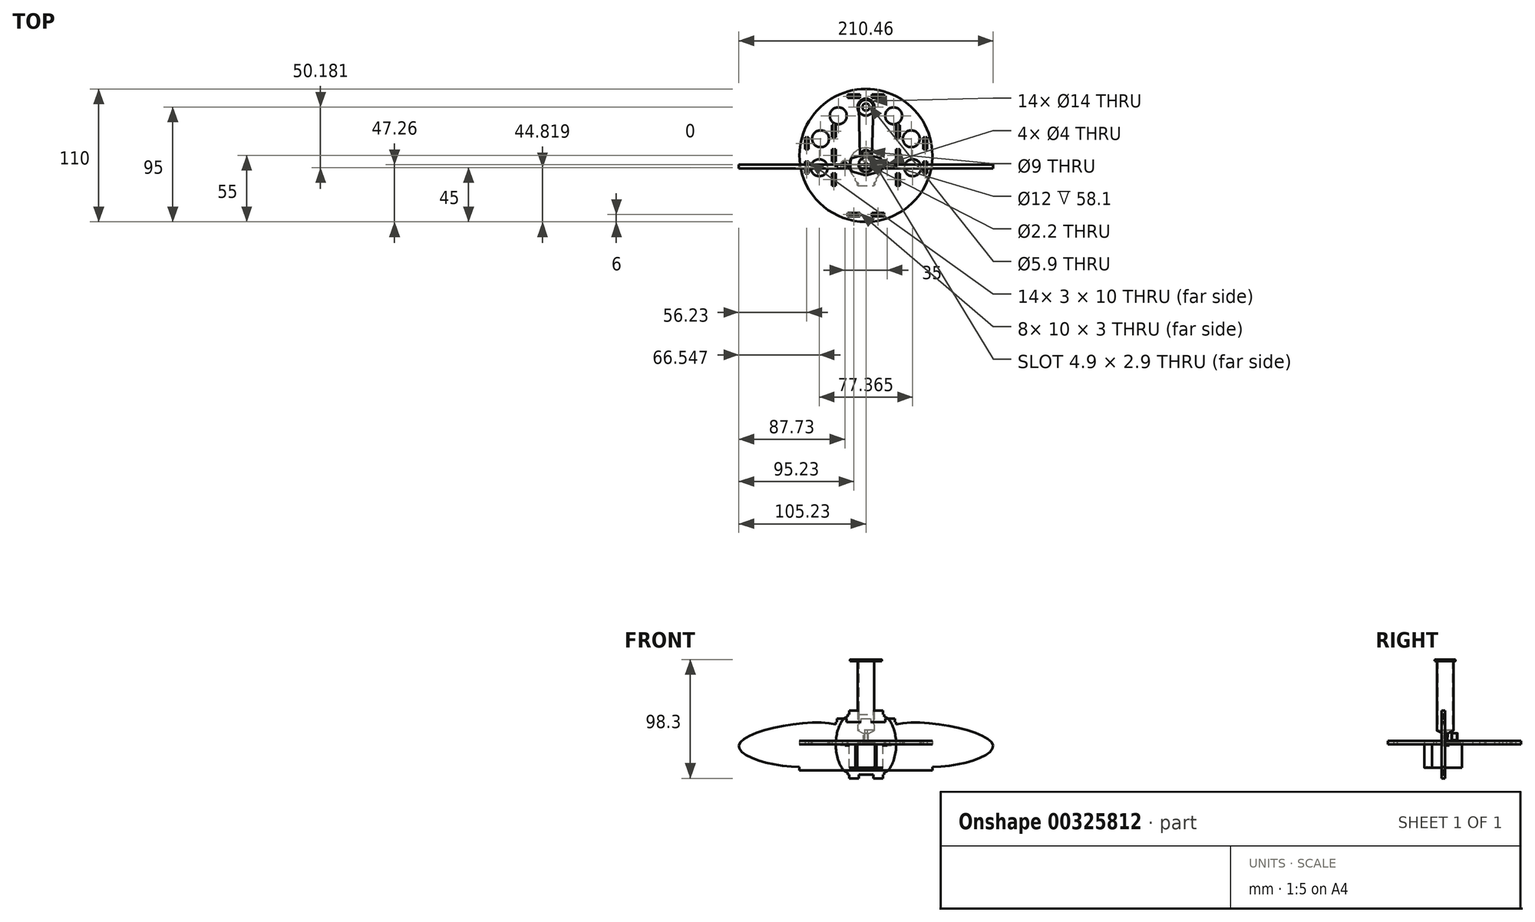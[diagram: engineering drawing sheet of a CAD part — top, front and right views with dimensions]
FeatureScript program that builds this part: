
annotation { "Feature Type Name" : "Feature", "Feature Type Description" : "" }
export const myFeature = defineFeature(function(context is Context, id is Id, definition is map)
    precondition{}
    {
        {
            var Q0;
            Q0=qCreatedBy(makeId("Top.planeOp"),FACE);
            var sketch = newSketch(context, id + "F0", { "sketchPlane" : qUnion([Q0])});
            skCircle(sketch, "E0", {"center": v(0, 0) * mm, "radius": 6.85 * mm});
            skCircle(sketch, "E1", {"center": v(0, 0) * mm, "radius": 1.1 * mm});
            skCircle(sketch, "E2", {"center": v(0, 0) * mm, "radius": 8.5 * mm});
            skLineSegment(sketch, "E3", {"start": v(-1.1, 0) * mm, "end": v(1.1, 0) * mm});
            skLineSegment(sketch, "E4", {"start": v(-11.5, 5.5) * mm, "end": v(-11.4, 5.5) * mm});
            skLineSegment(sketch, "E5", {"start": v(11.5, -5.5) * mm, "end": v(11.4, -5.5) * mm});
            skLineSegment(sketch, "E6", {"start": v(-11.5, 5.5) * mm, "end": v(-2.38, 8.16) * mm});
            skLineSegment(sketch, "E7", {"start": v(-11.5, -5.5) * mm, "end": v(-2.38, -8.16) * mm});
            skLineSegment(sketch, "E8", {"start": v(11.5, -5.5) * mm, "end": v(2.38, -8.16) * mm});
            skLineSegment(sketch, "E9", {"start": v(11.5, 5.5) * mm, "end": v(2.38, 8.16) * mm});
            skFitSpline(sketch, "E10", {"points": [v(-11.5, 5.5) * mm, v(-13.25, 0) * mm, v(-11.5, -5.5) * mm, v(-8.5, 0) * mm, v(-11.5, 5.5) * mm]});
            skFitSpline(sketch, "E11", {"points": [v(11.5, 5.5) * mm, v(13.25, 0) * mm, v(11.5, -5.5) * mm, v(8.5, 0) * mm, v(11.5, 5.5) * mm]});
            skLineSegment(sketch, "E12.trimOffspring", {"start": v(-11.4, -5.5) * mm, "end": v(-11.5, -5.5) * mm});
            skLineSegment(sketch, "E13.trimOffspring", {"start": v(11.4, 5.5) * mm, "end": v(11.5, 5.5) * mm});
            skCircle(sketch, "E14", {"center": v(0, 0) * mm, "radius": 6 * mm});
            skCircle(sketch, "E15", {"center": v(0, 0) * mm, "radius": 2 * mm});
            skSolve(sketch);
        }
        {
            var Q0;
            Q0 = qSketchRegion(id + "F0", true);
            extrude(context, id + "F1", {"entities" : qUnion([Q0]), "depth" : 70.3 * mm});
        }
        {
            var Q0;
            Q0 = qSketchRegion(id + "F0", true);
            extrude(context, id + "F2", {"entities" : qUnion([Q0]), "operationType" : NewBodyOperationType.REMOVE, "depth" : (70.3 - 1.4) * mm});
        }
        {
            var Q0;
            Q0=makeQuery(id+"F0.imprint","IMPRINT",FACE,{"disambiguationData":[TD([[makeQuery(id+"F0.imprint","IMPRINT",EDGE,{"derivedFrom":sQuery(id+"F0.wireOp",EDGE,"E0")}),1.0]])]});
            extrude(context, id + "F3", {"entities" : qUnion([Q0]), "operationType" : NewBodyOperationType.ADD, "depth" : 70.3 * mm, "hasSecondDirection" : true, "secondDirectionOppositeDirection" : true, "secondDirectionDepth" : -9 * mm});
        }
        {
            var Q0;
            Q0=makeQuery(id+"F0.imprint","IMPRINT",FACE,{"disambiguationData":[TD([[makeQuery(id+"F0.imprint","IMPRINT",EDGE,{"derivedFrom":sQuery(id+"F0.wireOp",EDGE,"E14")}),1.0]])]});
            extrude(context, id + "F4", {"entities" : qUnion([Q0]), "operationType" : NewBodyOperationType.ADD, "depth" : 12 * mm, "hasSecondDirection" : true, "secondDirectionOppositeDirection" : true, "secondDirectionDepth" : -9 * mm});
        }
        {
            var Q0;
            Q0=makeQuery(id+"F0.imprint","IMPRINT",FACE,{"disambiguationData":[TD([[makeQuery(id+"F0.imprint","IMPRINT",EDGE,{"derivedFrom":sQuery(id+"F0.wireOp",EDGE,"E15")}),1.0]])]});
            extrude(context, id + "F5", {"entities" : qUnion([Q0]), "operationType" : NewBodyOperationType.ADD, "depth" : 12 * mm});
        }
        {
            var Q0;
            Q0=makeQuery(id+"F3.opExtrude","CAP_EDGE",EDGE,{"disambiguationData":[OSD([sQuery(id+"F0.wireOp",EDGE,"E0")])],"isStart":true});
            chamfer(context, id + "F6", {"entities" : qUnion([Q0]), "chamferType" : ChamferType.TWO_OFFSETS, "width1" : 2.5 * mm, "oppositeDirection" : false, "width2" : 4.9 * mm, "tangentPropagation" : true});
        }
        {
            var Q0;
            Q0=makeQuery(id+"F5.opExtrude","CAP_EDGE",EDGE,{"disambiguationData":[OSD([sQuery(id+"F0.wireOp",EDGE,"E15")])],"isStart":true});
            chamfer(context, id + "F7", {"entities" : qUnion([Q0]), "chamferType" : ChamferType.TWO_OFFSETS, "width1" : 9 * mm, "oppositeDirection" : false, "width2" : 0.1 * mm, "tangentPropagation" : true});
        }
        {
            var Q0;
            Q0=makeQuery(id+"F5.opExtrude","CAP_EDGE",EDGE,{"disambiguationData":[OSD([sQuery(id+"F0.wireOp",EDGE,"E1")])],"isStart":true});
            var Q1;
            {var subQ0=sQuery(id+"F0.wireOp",EDGE,"E15");Q1=makeQuery(id+"F7.opChamfer","BLEND_EDGE",EDGE,{"blendedFrom":[makeQuery(id+"F5.opExtrude","CAP_EDGE",EDGE,{"disambiguationData":[OSD([subQ0])],"isStart":true}),makeQuery(id+"F5.opExtrude","CAP_FACE",FACE,{"disambiguationData":[OSD([sQuery(id+"F0.wireOp",EDGE,"E1"),subQ0])],"isStart":true})],"blendedInto":[makeQuery(id+"F5.opExtrude","CAP_FACE",FACE,{"disambiguationData":[OSD([sQuery(id+"F0.wireOp",EDGE,"E1"),subQ0])],"isStart":true})]});}
            var Q2;
            {var subQ0=sQuery(id+"F0.wireOp",EDGE,"E0");Q2=makeQuery(id+"F6.opChamfer","BLEND_EDGE",EDGE,{"blendedFrom":[makeQuery(id+"F3.opExtrude","CAP_EDGE",EDGE,{"disambiguationData":[OSD([subQ0])],"isStart":true}),makeQuery(id+"F3.opExtrude","SWEPT_FACE",FACE,{"disambiguationData":[OSD([subQ0])]})],"blendedInto":[makeQuery(id+"F3.opExtrude","SWEPT_FACE",FACE,{"disambiguationData":[OSD([subQ0])]})]});}
            var Q3;
            {var subQ0=sQuery(id+"F0.wireOp",EDGE,"E15");Q3=makeQuery(id+"F7.opChamfer","BLEND_EDGE",EDGE,{"blendedFrom":[makeQuery(id+"F5.opExtrude","CAP_EDGE",EDGE,{"disambiguationData":[OSD([subQ0])],"isStart":true}),makeQuery(id+"F5.opExtrude","SWEPT_FACE",FACE,{"disambiguationData":[OSD([subQ0])]})],"blendedInto":[makeQuery(id+"F5.opExtrude","SWEPT_FACE",FACE,{"disambiguationData":[OSD([subQ0])]})]});}
            var Q4;
            Q4=makeQuery(id+"F3.opExtrude","CAP_EDGE",EDGE,{"disambiguationData":[OSD([sQuery(id+"F0.wireOp",EDGE,"E14")])],"isStart":false});
            var Q5;
            Q5=makeQuery(id+"F1.opExtrude","CAP_EDGE",EDGE,{"disambiguationData":[OSD([sQuery(id+"F0.wireOp",EDGE,"E9")])],"isStart":false});
            var Q6;
            Q6=makeQuery(id+"F1.opExtrude","CAP_EDGE",EDGE,{"disambiguationData":[OSD([sQuery(id+"F0.wireOp",EDGE,"E11")])],"isStart":false});
            var Q7;
            Q7=makeQuery(id+"F1.opExtrude","CAP_EDGE",EDGE,{"disambiguationData":[OSD([sQuery(id+"F0.wireOp",EDGE,"E8")])],"isStart":false});
            var Q8;
            {var subQ0=sQuery(id+"F0.wireOp",EDGE,"E2");Q8=makeQuery(id+"F1.opExtrude","CAP_EDGE",EDGE,{"disambiguationData":[OSD([subQ0]),TDD([makeQuery(id+"F0.imprint","IMPRINT",EDGE,{"disambiguationData":[TD([[makeQuery(id+"F0.imprint","INTERSECT",VERTEX,{"derivedFrom":[subQ0,sQuery(id+"F0.wireOp",EDGE,"E7")]}),-1.0]])],"derivedFrom":subQ0})])],"isStart":false});}
            var Q9;
            Q9=makeQuery(id+"F1.opExtrude","CAP_EDGE",EDGE,{"disambiguationData":[OSD([sQuery(id+"F0.wireOp",EDGE,"E7")])],"isStart":false});
            var Q10;
            Q10=makeQuery(id+"F1.opExtrude","CAP_EDGE",EDGE,{"disambiguationData":[OSD([sQuery(id+"F0.wireOp",EDGE,"E10")])],"isStart":false});
            var Q11;
            Q11=makeQuery(id+"F1.opExtrude","CAP_EDGE",EDGE,{"disambiguationData":[OSD([sQuery(id+"F0.wireOp",EDGE,"E6")])],"isStart":false});
            var Q12;
            {var subQ0=sQuery(id+"F0.wireOp",EDGE,"E2");Q12=makeQuery(id+"F1.opExtrude","CAP_EDGE",EDGE,{"disambiguationData":[OSD([subQ0]),TDD([makeQuery(id+"F0.imprint","IMPRINT",EDGE,{"disambiguationData":[TD([[makeQuery(id+"F0.imprint","INTERSECT",VERTEX,{"derivedFrom":[subQ0,sQuery(id+"F0.wireOp",EDGE,"E6")]}),1.0]])],"derivedFrom":subQ0})])],"isStart":false});}
            var Q13;
            Q13=makeQuery(id+"F2.boolean.opBoolean","COPY",EDGE,{"derivedFrom":makeQuery(id+"F2.opExtrude","CAP_EDGE",EDGE,{"disambiguationData":[OSD([sQuery(id+"F0.wireOp",EDGE,"E7")])],"isStart":false})});
            var Q14;
            {var subQ0=sQuery(id+"F0.wireOp",EDGE,"E2");Q14=makeQuery(id+"F2.boolean.opBoolean","COPY",EDGE,{"derivedFrom":makeQuery(id+"F2.opExtrude","CAP_EDGE",EDGE,{"disambiguationData":[OSD([subQ0]),TDD([makeQuery(id+"F0.imprint","IMPRINT",EDGE,{"disambiguationData":[TD([[makeQuery(id+"F0.imprint","INTERSECT",VERTEX,{"derivedFrom":[subQ0,sQuery(id+"F0.wireOp",EDGE,"E7")]}),-1.0]])],"derivedFrom":subQ0})])],"isStart":false})});}
            var Q15;
            Q15=makeQuery(id+"F2.boolean.opBoolean","COPY",EDGE,{"derivedFrom":makeQuery(id+"F2.opExtrude","CAP_EDGE",EDGE,{"disambiguationData":[OSD([sQuery(id+"F0.wireOp",EDGE,"E8")])],"isStart":false})});
            var Q16;
            Q16=makeQuery(id+"F2.boolean.opBoolean","COPY",EDGE,{"derivedFrom":makeQuery(id+"F2.opExtrude","CAP_EDGE",EDGE,{"disambiguationData":[OSD([sQuery(id+"F0.wireOp",EDGE,"E11")])],"isStart":false})});
            var Q17;
            Q17=makeQuery(id+"F2.boolean.opBoolean","COPY",EDGE,{"derivedFrom":makeQuery(id+"F2.opExtrude","CAP_EDGE",EDGE,{"disambiguationData":[OSD([sQuery(id+"F0.wireOp",EDGE,"E9")])],"isStart":false})});
            var Q18;
            Q18=makeQuery(id+"F2.boolean.opBoolean","COPY",EDGE,{"derivedFrom":makeQuery(id+"F2.opExtrude","CAP_EDGE",EDGE,{"disambiguationData":[OSD([sQuery(id+"F0.wireOp",EDGE,"E10")])],"isStart":false})});
            var Q19;
            Q19=makeQuery(id+"F2.boolean.opBoolean","COPY",EDGE,{"derivedFrom":makeQuery(id+"F2.opExtrude","CAP_EDGE",EDGE,{"disambiguationData":[OSD([sQuery(id+"F0.wireOp",EDGE,"E6")])],"isStart":false})});
            var Q20;
            {var subQ0=sQuery(id+"F0.wireOp",EDGE,"E2");Q20=makeQuery(id+"F2.boolean.opBoolean","COPY",EDGE,{"derivedFrom":makeQuery(id+"F2.opExtrude","CAP_EDGE",EDGE,{"disambiguationData":[OSD([subQ0]),TDD([makeQuery(id+"F0.imprint","IMPRINT",EDGE,{"disambiguationData":[TD([[makeQuery(id+"F0.imprint","INTERSECT",VERTEX,{"derivedFrom":[subQ0,sQuery(id+"F0.wireOp",EDGE,"E6")]}),1.0]])],"derivedFrom":subQ0})])],"isStart":false})});}
            var Q21;
            Q21=makeQuery(id+"F2.boolean.opBoolean","COPY",EDGE,{"derivedFrom":makeQuery(id+"F2.opExtrude","CAP_EDGE",EDGE,{"disambiguationData":[OSD([sQuery(id+"F0.wireOp",EDGE,"E0")])],"isStart":false})});
            fillet(context, id + "F8", {"entities" : qUnion([Q0, Q1, Q2, Q3, Q4, Q5, Q6, Q7, Q8, Q9, Q10, Q11, Q12, Q13, Q14, Q15, Q16, Q17, Q18, Q19, Q20, Q21]), "radius" : 0.2 * mm, "tangentPropagation" : true, "allowEdgeOverflow" : false});
        }
        {
            var Q0;
            Q0=qCreatedBy(makeId("Top.planeOp"),FACE);
            var sketch = newSketch(context, id + "F9", { "sketchPlane" : qUnion([Q0])});
            skCircle(sketch, "E16", {"center": v(0, 0) * mm, "radius": 14 * mm});
            skLineSegment(sketch, "E17", {"start": v(0, 0) * mm, "end": v(0, -13.2) * mm, "construction": true});
            skLineSegment(sketch, "E18", {"start": v(-7.3, -17.2) * mm, "end": v(7.3, -17.2) * mm});
            skLineSegment(sketch, "E19", {"start": v(-7.3, -14.7) * mm, "end": v(7.3, -14.7) * mm, "construction": true});
            skLineSegment(sketch, "E20", {"start": v(7.3, -17.2) * mm, "end": v(7.3, -14.7) * mm});
            skLineSegment(sketch, "E21", {"start": v(-7.3, -17.2) * mm, "end": v(-7.3, -14.7) * mm});
            skLineSegment(sketch, "E22", {"start": v(-8.75, -13.2) * mm, "end": v(-4.66, -13.2) * mm, "construction": true});
            skLineSegment(sketch, "E23", {"start": v(0, -14.7) * mm, "end": v(0, -13.2) * mm});
            skLineSegment(sketch, "E24", {"start": v(7.3, -14.7) * mm, "end": v(8.75, -13.2) * mm});
            skLineSegment(sketch, "E25", {"start": v(8.75, -13.2) * mm, "end": v(8.75, -10.93) * mm});
            skLineSegment(sketch, "E26", {"start": v(-7.3, -14.7) * mm, "end": v(-8.75, -13.2) * mm});
            skLineSegment(sketch, "E27", {"start": v(-8.75, -13.2) * mm, "end": v(-8.75, -10.93) * mm});
            skLineSegment(sketch, "E28", {"start": v(-17.5, 0) * mm, "end": v(17.5, 0) * mm, "construction": true});
            skCircle(sketch, "E29", {"center": v(-17.5, 0) * mm, "radius": 2 * mm});
            skCircle(sketch, "E30", {"center": v(17.5, 0) * mm, "radius": 2 * mm});
            skArc(sketch, "E31", {"start": v(-17.5, 3.5) * mm, "mid": v(-21, 0) * mm, "end": v(-17.5, -3.5) * mm});
            skArc(sketch, "E32", {"start": v(17.5, -3.5) * mm, "mid": v(21, 0) * mm, "end": v(17.5, 3.5) * mm});
            skLineSegment(sketch, "E33", {"start": v(-17.5, 3.5) * mm, "end": v(-13.56, 3.5) * mm});
            skLineSegment(sketch, "E34", {"start": v(-17.5, -3.5) * mm, "end": v(-13.56, -3.5) * mm});
            skLineSegment(sketch, "E35", {"start": v(17.5, -3.5) * mm, "end": v(13.56, -3.5) * mm});
            skLineSegment(sketch, "E36", {"start": v(17.5, 3.5) * mm, "end": v(13.56, 3.5) * mm});
            skCircle(sketch, "E37", {"center": v(0, 7.74) * mm, "radius": 4.5 * mm});
            skCircle(sketch, "E38", {"center": v(0, 7.74) * mm, "radius": 2.45 * mm});
            skLineSegment(sketch, "E39.trimOffspring", {"start": v(4.66, -13.2) * mm, "end": v(8.75, -13.2) * mm, "construction": true});
            skLineSegment(sketch, "E40.trimOffspring", {"start": v(0, -14) * mm, "end": v(0, -17.2) * mm, "construction": true});
            skLineSegment(sketch, "E41", {"start": v(-1.45, 7.74) * mm, "end": v(1.45, 7.74) * mm, "construction": true});
            skLineSegment(sketch, "E42", {"start": v(-1.45, 9.71) * mm, "end": v(-1.45, 5.77) * mm});
            skLineSegment(sketch, "E43", {"start": v(1.45, 9.71) * mm, "end": v(1.45, 5.77) * mm});
            skSolve(sketch);
        }
        {
            var Q0;
            Q0=makeQuery(id+"F9.imprint","IMPRINT",FACE,{"disambiguationData":[TD([[makeQuery(id+"F9.imprint","IMPRINT",EDGE,{"derivedFrom":sQuery(id+"F9.wireOp",EDGE,"E29")}),-1.0]])]});
            var Q1;
            Q1=makeQuery(id+"F9.imprint","IMPRINT",FACE,{"disambiguationData":[TD([[makeQuery(id+"F9.imprint","IMPRINT",EDGE,{"derivedFrom":sQuery(id+"F9.wireOp",EDGE,"E37")}),-1.0]])]});
            var Q2;
            Q2=makeQuery(id+"F9.imprint","IMPRINT",FACE,{"disambiguationData":[TD([[makeQuery(id+"F9.imprint","IMPRINT",EDGE,{"derivedFrom":sQuery(id+"F9.wireOp",EDGE,"E18")}),1.0]])]});
            var Q3;
            Q3=makeQuery(id+"F9.imprint","IMPRINT",FACE,{"disambiguationData":[TD([[makeQuery(id+"F9.imprint","IMPRINT",EDGE,{"derivedFrom":sQuery(id+"F9.wireOp",EDGE,"E30")}),-1.0]])]});
            var Q4;
            Q4=makeQuery(id+"F9.imprint","IMPRINT",FACE,{"disambiguationData":[TD([[makeQuery(id+"F9.imprint","IMPRINT",EDGE,{"derivedFrom":sQuery(id+"F9.wireOp",EDGE,"E37")}),1.0]])]});
            var Q5;
            {var subQ0=sQuery(id+"F9.wireOp",EDGE,"E42");Q5=makeQuery(id+"F9.imprint","IMPRINT",FACE,{"disambiguationData":[TD([[makeQuery(id+"F9.imprint","IMPRINT",EDGE,{"derivedFrom":subQ0}),1.0]])]});}
            var Q6;
            {var subQ0=sQuery(id+"F9.wireOp",EDGE,"E42");Q6=makeQuery(id+"F9.imprint","IMPRINT",FACE,{"disambiguationData":[TD([[makeQuery(id+"F9.imprint","IMPRINT",EDGE,{"derivedFrom":subQ0}),-1.0]])]});}
            var Q7;
            {var subQ0=sQuery(id+"F9.wireOp",EDGE,"E43");Q7=makeQuery(id+"F9.imprint","IMPRINT",FACE,{"disambiguationData":[TD([[makeQuery(id+"F9.imprint","IMPRINT",EDGE,{"derivedFrom":subQ0}),1.0]])]});}
            extrude(context, id + "F10", {"entities" : qUnion([Q0, Q1, Q2, Q3, Q4, Q5, Q6, Q7]), "oppositeDirection" : true, "depth" : 19.3 * mm});
        }
        {
            var Q0;
            Q0=makeQuery(id+"F9.imprint","IMPRINT",FACE,{"disambiguationData":[TD([[makeQuery(id+"F9.imprint","IMPRINT",EDGE,{"derivedFrom":sQuery(id+"F9.wireOp",EDGE,"E29")}),-1.0]])]});
            var Q1;
            Q1=makeQuery(id+"F9.imprint","IMPRINT",FACE,{"disambiguationData":[TD([[makeQuery(id+"F9.imprint","IMPRINT",EDGE,{"derivedFrom":sQuery(id+"F9.wireOp",EDGE,"E30")}),-1.0]])]});
            extrude(context, id + "F11", {"entities" : qUnion([Q0, Q1]), "operationType" : NewBodyOperationType.REMOVE, "endBound" : BoundingType.THROUGH_ALL, "oppositeDirection" : true, "depth" : 25 * mm, "hasSecondDirection" : true, "secondDirectionOppositeDirection" : false, "secondDirectionDepth" : -0.8 * mm});
        }
        {
            var Q0;
            Q0=makeQuery(id+"F9.imprint","IMPRINT",FACE,{"disambiguationData":[TD([[makeQuery(id+"F9.imprint","IMPRINT",EDGE,{"derivedFrom":sQuery(id+"F9.wireOp",EDGE,"E37")}),1.0]])]});
            extrude(context, id + "F12", {"entities" : qUnion([Q0]), "operationType" : NewBodyOperationType.ADD, "depth" : 1.5 * mm});
        }
        {
            var Q0;
            {var subQ0=sQuery(id+"F9.wireOp",EDGE,"E42");Q0=makeQuery(id+"F9.imprint","IMPRINT",FACE,{"disambiguationData":[TD([[makeQuery(id+"F9.imprint","IMPRINT",EDGE,{"derivedFrom":subQ0}),-1.0]])]});}
            var Q1;
            {var subQ0=sQuery(id+"F9.wireOp",EDGE,"E43");Q1=makeQuery(id+"F9.imprint","IMPRINT",FACE,{"disambiguationData":[TD([[makeQuery(id+"F9.imprint","IMPRINT",EDGE,{"derivedFrom":subQ0}),1.0]])]});}
            extrude(context, id + "F13", {"entities" : qUnion([Q0, Q1]), "operationType" : NewBodyOperationType.ADD, "depth" : 3.5 * mm});
        }
        {
            var Q0;
            {var subQ0=sQuery(id+"F9.wireOp",EDGE,"E42");Q0=makeQuery(id+"F9.imprint","IMPRINT",FACE,{"disambiguationData":[TD([[makeQuery(id+"F9.imprint","IMPRINT",EDGE,{"derivedFrom":subQ0}),1.0]])]});}
            extrude(context, id + "F14", {"entities" : qUnion([Q0]), "operationType" : NewBodyOperationType.ADD, "depth" : 9.5 * mm});
        }
        {
            var Q0;
            Q0=makeQuery(id+"F10.opExtrude","CAP_EDGE",EDGE,{"disambiguationData":[OSD([sQuery(id+"F9.wireOp",EDGE,"E18")])],"isStart":false});
            var Q1;
            {var subQ0=sQuery(id+"F9.wireOp",EDGE,"E38");Q1=makeQuery(id+"F14.opExtrude","CAP_EDGE",EDGE,{"disambiguationData":[OSD([subQ0]),TDD([makeQuery(id+"F9.imprint","IMPRINT",EDGE,{"disambiguationData":[TD([[makeQuery(id+"F9.imprint","INTERSECT",VERTEX,{"disambiguationData":[OD(1.0)],"derivedFrom":[subQ0,sQuery(id+"F9.wireOp",EDGE,"E42")]}),-1.0]])],"derivedFrom":subQ0})])],"isStart":false});}
            var Q2;
            {var subQ0=sQuery(id+"F9.wireOp",EDGE,"E42");var subQ1=sQuery(id+"F9.wireOp",EDGE,"E38");Q2=makeQuery(id+"F13.opExtrude","CAP_EDGE",EDGE,{"disambiguationData":[OSD([subQ1]),TDD([makeQuery(id+"F9.imprint","IMPRINT",EDGE,{"disambiguationData":[TD([[makeQuery(id+"F9.imprint","INTERSECT",VERTEX,{"disambiguationData":[OD(0.0)],"derivedFrom":[subQ1,subQ0]}),-1.0]])],"derivedFrom":subQ1})])],"isStart":false});}
            var Q3;
            {var subQ0=sQuery(id+"F9.wireOp",EDGE,"E43");var subQ1=sQuery(id+"F9.wireOp",EDGE,"E38");Q3=makeQuery(id+"F13.opExtrude","CAP_EDGE",EDGE,{"disambiguationData":[OSD([subQ1]),TDD([makeQuery(id+"F9.imprint","IMPRINT",EDGE,{"disambiguationData":[TD([[makeQuery(id+"F9.imprint","INTERSECT",VERTEX,{"disambiguationData":[OD(0.0)],"derivedFrom":[subQ1,subQ0]}),1.0]])],"derivedFrom":subQ1})])],"isStart":false});}
            var Q4;
            {var subQ0=sQuery(id+"F9.wireOp",EDGE,"E38");Q4=makeQuery(id+"F14.opExtrude","CAP_EDGE",EDGE,{"disambiguationData":[OSD([subQ0]),TDD([makeQuery(id+"F9.imprint","IMPRINT",EDGE,{"disambiguationData":[TD([[makeQuery(id+"F9.imprint","INTERSECT",VERTEX,{"disambiguationData":[OD(0.0)],"derivedFrom":[subQ0,sQuery(id+"F9.wireOp",EDGE,"E42")]}),1.0]])],"derivedFrom":subQ0})])],"isStart":false});}
            fillet(context, id + "F15", {"entities" : qUnion([Q0, Q1, Q2, Q3, Q4]), "radius" : 0.3 * mm, "tangentPropagation" : true, "allowEdgeOverflow" : false});
        }
        {
            var Q0;
            Q0=makeQuery(id+"F10.opExtrude","SWEPT_EDGE",EDGE,{"disambiguationData":[OSD([sQuery(id+"F9.wireOp",EDGE,"E18"),sQuery(id+"F9.wireOp",EDGE,"E20")])]});
            var Q1;
            Q1=makeQuery(id+"F10.opExtrude","SWEPT_EDGE",EDGE,{"disambiguationData":[OSD([sQuery(id+"F9.wireOp",EDGE,"E18"),sQuery(id+"F9.wireOp",EDGE,"E21")])]});
            var Q2;
            {var subQ0=sQuery(id+"F9.wireOp",EDGE,"E18");Q2=makeQuery(id+"F15.opFillet","BLEND_EDGE",EDGE,{"blendedFrom":[makeQuery(id+"F10.opExtrude","CAP_EDGE",EDGE,{"disambiguationData":[OSD([subQ0])],"isStart":false}),makeQuery(id+"F10.opExtrude","SWEPT_FACE",FACE,{"disambiguationData":[OSD([subQ0])]})],"blendedInto":[makeQuery(id+"F10.opExtrude","SWEPT_FACE",FACE,{"disambiguationData":[OSD([subQ0])]})]});}
            fillet(context, id + "F16", {"entities" : qUnion([Q0, Q1, Q2]), "radius" : 1 * mm, "tangentPropagation" : true, "allowEdgeOverflow" : false});
        }
        {
            var Q0;
            Q0=makeQuery(id+"F10.opExtrude","SWEPT_EDGE",EDGE,{"disambiguationData":[OSD([sQuery(id+"F9.wireOp",EDGE,"E26"),sQuery(id+"F9.wireOp",EDGE,"E27")])]});
            var Q1;
            Q1=makeQuery(id+"F10.opExtrude","SWEPT_EDGE",EDGE,{"disambiguationData":[OSD([sQuery(id+"F9.wireOp",EDGE,"E21"),sQuery(id+"F9.wireOp",EDGE,"E26")])]});
            var Q2;
            Q2=makeQuery(id+"F10.opExtrude","SWEPT_EDGE",EDGE,{"disambiguationData":[OSD([sQuery(id+"F9.wireOp",EDGE,"E24"),sQuery(id+"F9.wireOp",EDGE,"E25")])]});
            var Q3;
            Q3=makeQuery(id+"F10.opExtrude","SWEPT_EDGE",EDGE,{"disambiguationData":[OSD([sQuery(id+"F9.wireOp",EDGE,"E20"),sQuery(id+"F9.wireOp",EDGE,"E24")])]});
            var Q4;
            Q4=makeQuery(id+"F16.opFillet","BLEND_EDGE",EDGE,{"blendedFrom":[makeQuery(id+"F10.opExtrude","CAP_EDGE",EDGE,{"disambiguationData":[OSD([sQuery(id+"F9.wireOp",EDGE,"E20")])],"isStart":false}),makeQuery(id+"F10.opExtrude","SWEPT_FACE",FACE,{"disambiguationData":[OSD([sQuery(id+"F9.wireOp",EDGE,"E24")])]})],"blendedInto":[makeQuery(id+"F10.opExtrude","SWEPT_FACE",FACE,{"disambiguationData":[OSD([sQuery(id+"F9.wireOp",EDGE,"E24")])]})]});
            var Q5;
            Q5=makeQuery(id+"F16.opFillet","BLEND_EDGE",EDGE,{"blendedFrom":[makeQuery(id+"F10.opExtrude","CAP_EDGE",EDGE,{"disambiguationData":[OSD([sQuery(id+"F9.wireOp",EDGE,"E21")])],"isStart":false}),makeQuery(id+"F10.opExtrude","SWEPT_FACE",FACE,{"disambiguationData":[OSD([sQuery(id+"F9.wireOp",EDGE,"E26")])]})],"blendedInto":[makeQuery(id+"F10.opExtrude","SWEPT_FACE",FACE,{"disambiguationData":[OSD([sQuery(id+"F9.wireOp",EDGE,"E26")])]})]});
            var Q6;
            Q6=makeQuery(id+"F10.opExtrude","CAP_EDGE",EDGE,{"disambiguationData":[OSD([sQuery(id+"F9.wireOp",EDGE,"E24")])],"isStart":false});
            var Q7;
            Q7=makeQuery(id+"F10.opExtrude","CAP_EDGE",EDGE,{"disambiguationData":[OSD([sQuery(id+"F9.wireOp",EDGE,"E26")])],"isStart":false});
            fillet(context, id + "F17", {"entities" : qUnion([Q0, Q1, Q2, Q3, Q4, Q5, Q6, Q7]), "radius" : 0.3 * mm, "tangentPropagation" : true, "allowEdgeOverflow" : false});
        }
        {
            var Q0;
            Q0=qCreatedBy(makeId("Top.planeOp"),FACE);
            var sketch = newSketch(context, id + "F18", { "sketchPlane" : qUnion([Q0])});
            skCircle(sketch, "E44.0", {"center": v(-17.5, 0) * mm, "radius": 2 * mm});
            skCircle(sketch, "E45.0", {"center": v(0, 7.74) * mm, "radius": 4.5 * mm});
            skCircle(sketch, "E46.0", {"center": v(17.5, 0) * mm, "radius": 2 * mm});
            skCircle(sketch, "E47", {"center": v(0, 7.74) * mm, "radius": 55 * mm});
            skCircle(sketch, "E48", {"center": v(0, 7.74) * mm, "radius": 40 * mm, "construction": true});
            skCircle(sketch, "E49", {"center": v(0, 47.74) * mm, "radius": 7 * mm});
            skCircle(sketch, "E50", {"center": v(-22.9, 40.54) * mm, "radius": 7 * mm});
            skCircle(sketch, "E51", {"center": v(-37.55, 21.53) * mm, "radius": 7 * mm});
            skCircle(sketch, "E52", {"center": v(22.9, 40.54) * mm, "radius": 7 * mm});
            skCircle(sketch, "E53", {"center": v(37.55, 21.53) * mm, "radius": 7 * mm});
            skCircle(sketch, "E54", {"center": v(38.68, -2.44) * mm, "radius": 7 * mm});
            skCircle(sketch, "E55", {"center": v(-38.68, -2.44) * mm, "radius": 7 * mm});
            skLineSegment(sketch, "E56", {"start": v(-49, 7.74) * mm, "end": v(49, 7.74) * mm, "construction": true});
            skLineSegment(sketch, "E57.bottom", {"start": v(-50.5, 2.74) * mm, "end": v(-47.5, 2.74) * mm});
            skLineSegment(sketch, "E57.top", {"start": v(-50.5, -7.26) * mm, "end": v(-47.5, -7.26) * mm});
            skLineSegment(sketch, "E57.left", {"start": v(-50.5, 2.74) * mm, "end": v(-50.5, -7.26) * mm});
            skLineSegment(sketch, "E57.right", {"start": v(-47.5, 2.74) * mm, "end": v(-47.5, -7.26) * mm});
            skLineSegment(sketch, "E58.bottom", {"start": v(47.5, 2.74) * mm, "end": v(50.5, 2.74) * mm});
            skLineSegment(sketch, "E58.top", {"start": v(47.5, -7.26) * mm, "end": v(50.5, -7.26) * mm});
            skLineSegment(sketch, "E58.left", {"start": v(47.5, 2.74) * mm, "end": v(47.5, -7.26) * mm});
            skLineSegment(sketch, "E58.right", {"start": v(50.5, 2.74) * mm, "end": v(50.5, -7.26) * mm});
            skLineSegment(sketch, "E59.bottom", {"start": v(-50.5, 22.74) * mm, "end": v(-47.5, 22.74) * mm});
            skLineSegment(sketch, "E59.top", {"start": v(-50.5, 12.74) * mm, "end": v(-47.5, 12.74) * mm});
            skLineSegment(sketch, "E59.left", {"start": v(-50.5, 22.74) * mm, "end": v(-50.5, 12.74) * mm});
            skLineSegment(sketch, "E59.right", {"start": v(-47.5, 22.74) * mm, "end": v(-47.5, 12.74) * mm});
            skLineSegment(sketch, "E60.bottom", {"start": v(47.5, 22.74) * mm, "end": v(50.5, 22.74) * mm});
            skLineSegment(sketch, "E60.top", {"start": v(47.5, 12.74) * mm, "end": v(50.5, 12.74) * mm});
            skLineSegment(sketch, "E60.left", {"start": v(47.5, 22.74) * mm, "end": v(47.5, 12.74) * mm});
            skLineSegment(sketch, "E60.right", {"start": v(50.5, 22.74) * mm, "end": v(50.5, 12.74) * mm});
            skLineSegment(sketch, "E61", {"start": v(0, 56.74) * mm, "end": v(0, -41.26) * mm, "construction": true});
            skLineSegment(sketch, "E62", {"start": v(-49, 12.74) * mm, "end": v(-49, 2.74) * mm, "construction": true});
            skLineSegment(sketch, "E63", {"start": v(49, 12.74) * mm, "end": v(49, 2.74) * mm, "construction": true});
            skLineSegment(sketch, "E64", {"start": v(-5, 56.74) * mm, "end": v(5, 56.74) * mm, "construction": true});
            skLineSegment(sketch, "E65", {"start": v(-5, -41.26) * mm, "end": v(5, -41.26) * mm, "construction": true});
            skLineSegment(sketch, "E66.bottom", {"start": v(-15, 58.24) * mm, "end": v(-5, 58.24) * mm});
            skLineSegment(sketch, "E66.top", {"start": v(-15, 55.24) * mm, "end": v(-5, 55.24) * mm});
            skLineSegment(sketch, "E66.left", {"start": v(-15, 58.24) * mm, "end": v(-15, 55.24) * mm});
            skLineSegment(sketch, "E66.right", {"start": v(-5, 58.24) * mm, "end": v(-5, 55.24) * mm});
            skLineSegment(sketch, "E67.bottom", {"start": v(5, 58.24) * mm, "end": v(15, 58.24) * mm});
            skLineSegment(sketch, "E67.top", {"start": v(5, 55.24) * mm, "end": v(15, 55.24) * mm});
            skLineSegment(sketch, "E67.left", {"start": v(5, 58.24) * mm, "end": v(5, 55.24) * mm});
            skLineSegment(sketch, "E67.right", {"start": v(15, 58.24) * mm, "end": v(15, 55.24) * mm});
            skLineSegment(sketch, "E68.bottom", {"start": v(5, -39.76) * mm, "end": v(15, -39.76) * mm});
            skLineSegment(sketch, "E68.top", {"start": v(5, -42.76) * mm, "end": v(15, -42.76) * mm});
            skLineSegment(sketch, "E68.left", {"start": v(5, -39.76) * mm, "end": v(5, -42.76) * mm});
            skLineSegment(sketch, "E68.right", {"start": v(15, -39.76) * mm, "end": v(15, -42.76) * mm});
            skLineSegment(sketch, "E69.bottom", {"start": v(-15, -39.76) * mm, "end": v(-5, -39.76) * mm});
            skLineSegment(sketch, "E69.top", {"start": v(-15, -42.76) * mm, "end": v(-5, -42.76) * mm});
            skLineSegment(sketch, "E69.left", {"start": v(-15, -39.76) * mm, "end": v(-15, -42.76) * mm});
            skLineSegment(sketch, "E69.right", {"start": v(-5, -39.76) * mm, "end": v(-5, -42.76) * mm});
            skSolve(sketch);
        }
        {
            var Q0;
            Q0 = qSketchRegion(id + "F18", true);
            extrude(context, id + "F19", {"entities" : qUnion([Q0]), "depth" : 3 * mm});
        }
        {
            var Q0;
            Q0=qCreatedBy(makeId("Top.planeOp"),FACE);
            var sketch = newSketch(context, id + "F20", { "sketchPlane" : qUnion([Q0])});
            skCircle(sketch, "E70.0.0", {"center": v(38.68, -2.44) * mm, "radius": 7 * mm});
            skCircle(sketch, "E71.0.0", {"center": v(37.55, 21.53) * mm, "radius": 7 * mm});
            skCircle(sketch, "E72.0.0", {"center": v(22.9, 40.54) * mm, "radius": 7 * mm});
            skLineSegment(sketch, "E73.0.0", {"start": v(5, 58.24) * mm, "end": v(5, 55.24) * mm});
            skLineSegment(sketch, "E73.0.1", {"start": v(5, 55.24) * mm, "end": v(15, 55.24) * mm});
            skLineSegment(sketch, "E73.0.2", {"start": v(15, 55.24) * mm, "end": v(15, 58.24) * mm});
            skLineSegment(sketch, "E73.0.3", {"start": v(15, 58.24) * mm, "end": v(5, 58.24) * mm});
            skLineSegment(sketch, "E74.0.0", {"start": v(-15, 58.24) * mm, "end": v(-15, 55.24) * mm});
            skLineSegment(sketch, "E74.0.1", {"start": v(-15, 55.24) * mm, "end": v(-5, 55.24) * mm});
            skLineSegment(sketch, "E74.0.2", {"start": v(-5, 55.24) * mm, "end": v(-5, 58.24) * mm});
            skLineSegment(sketch, "E74.0.3", {"start": v(-5, 58.24) * mm, "end": v(-15, 58.24) * mm});
            skCircle(sketch, "E75.0", {"center": v(0, 47.74) * mm, "radius": 7 * mm});
            skCircle(sketch, "E76.0", {"center": v(-22.9, 40.54) * mm, "radius": 7 * mm});
            skCircle(sketch, "E77.0", {"center": v(-37.55, 21.53) * mm, "radius": 7 * mm});
            skCircle(sketch, "E78.0", {"center": v(-38.68, -2.44) * mm, "radius": 7 * mm});
            skLineSegment(sketch, "E79.0.0", {"start": v(-50.5, 2.74) * mm, "end": v(-50.5, -7.26) * mm});
            skLineSegment(sketch, "E79.0.1", {"start": v(-50.5, -7.26) * mm, "end": v(-47.5, -7.26) * mm});
            skLineSegment(sketch, "E79.0.2", {"start": v(-47.5, -7.26) * mm, "end": v(-47.5, 2.74) * mm});
            skLineSegment(sketch, "E79.0.3", {"start": v(-47.5, 2.74) * mm, "end": v(-50.5, 2.74) * mm});
            skLineSegment(sketch, "E80.0.0", {"start": v(-50.5, 22.74) * mm, "end": v(-50.5, 12.74) * mm});
            skLineSegment(sketch, "E80.0.1", {"start": v(-50.5, 12.74) * mm, "end": v(-47.5, 12.74) * mm});
            skLineSegment(sketch, "E80.0.2", {"start": v(-47.5, 12.74) * mm, "end": v(-47.5, 22.74) * mm});
            skLineSegment(sketch, "E80.0.3", {"start": v(-47.5, 22.74) * mm, "end": v(-50.5, 22.74) * mm});
            skLineSegment(sketch, "E81.0.0", {"start": v(47.5, 22.74) * mm, "end": v(47.5, 12.74) * mm});
            skLineSegment(sketch, "E81.0.1", {"start": v(47.5, 12.74) * mm, "end": v(50.5, 12.74) * mm});
            skLineSegment(sketch, "E81.0.2", {"start": v(50.5, 12.74) * mm, "end": v(50.5, 22.74) * mm});
            skLineSegment(sketch, "E81.0.3", {"start": v(50.5, 22.74) * mm, "end": v(47.5, 22.74) * mm});
            skLineSegment(sketch, "E82.0.0", {"start": v(47.5, 2.74) * mm, "end": v(47.5, -7.26) * mm});
            skLineSegment(sketch, "E82.0.1", {"start": v(47.5, -7.26) * mm, "end": v(50.5, -7.26) * mm});
            skLineSegment(sketch, "E82.0.2", {"start": v(50.5, -7.26) * mm, "end": v(50.5, 2.74) * mm});
            skLineSegment(sketch, "E82.0.3", {"start": v(50.5, 2.74) * mm, "end": v(47.5, 2.74) * mm});
            skLineSegment(sketch, "E83.0.0", {"start": v(5, -39.76) * mm, "end": v(5, -42.76) * mm});
            skLineSegment(sketch, "E83.0.1", {"start": v(5, -42.76) * mm, "end": v(15, -42.76) * mm});
            skLineSegment(sketch, "E83.0.2", {"start": v(15, -42.76) * mm, "end": v(15, -39.76) * mm});
            skLineSegment(sketch, "E83.0.3", {"start": v(15, -39.76) * mm, "end": v(5, -39.76) * mm});
            skLineSegment(sketch, "E84.0.0", {"start": v(-15, -39.76) * mm, "end": v(-15, -42.76) * mm});
            skLineSegment(sketch, "E84.0.1", {"start": v(-15, -42.76) * mm, "end": v(-5, -42.76) * mm});
            skLineSegment(sketch, "E84.0.2", {"start": v(-5, -42.76) * mm, "end": v(-5, -39.76) * mm});
            skLineSegment(sketch, "E84.0.3", {"start": v(-5, -39.76) * mm, "end": v(-15, -39.76) * mm});
            skCircle(sketch, "E85.0", {"center": v(0, 7.74) * mm, "radius": 55 * mm});
            skLineSegment(sketch, "E86", {"start": v(-25, 7.74) * mm, "end": v(25, 7.74) * mm, "construction": true});
            skLineSegment(sketch, "E87.bottom", {"start": v(-28, 12.74) * mm, "end": v(-25, 12.74) * mm});
            skLineSegment(sketch, "E87.top", {"start": v(-28, 2.74) * mm, "end": v(-25, 2.74) * mm});
            skLineSegment(sketch, "E87.left", {"start": v(-28, 12.74) * mm, "end": v(-28, 2.74) * mm});
            skLineSegment(sketch, "E87.right", {"start": v(-25, 12.74) * mm, "end": v(-25, 2.74) * mm});
            skLineSegment(sketch, "E88.bottom", {"start": v(-28, -7.26) * mm, "end": v(-25, -7.26) * mm});
            skLineSegment(sketch, "E88.top", {"start": v(-28, -17.26) * mm, "end": v(-25, -17.26) * mm});
            skLineSegment(sketch, "E88.left", {"start": v(-28, -7.26) * mm, "end": v(-28, -17.26) * mm});
            skLineSegment(sketch, "E88.right", {"start": v(-25, -7.26) * mm, "end": v(-25, -17.26) * mm});
            skLineSegment(sketch, "E89.bottom", {"start": v(-28, 32.74) * mm, "end": v(-25, 32.74) * mm});
            skLineSegment(sketch, "E89.top", {"start": v(-28, 22.74) * mm, "end": v(-25, 22.74) * mm});
            skLineSegment(sketch, "E89.left", {"start": v(-28, 32.74) * mm, "end": v(-28, 22.74) * mm});
            skLineSegment(sketch, "E89.right", {"start": v(-25, 32.74) * mm, "end": v(-25, 22.74) * mm});
            skLineSegment(sketch, "E90.bottom", {"start": v(25, 12.74) * mm, "end": v(28, 12.74) * mm});
            skLineSegment(sketch, "E90.top", {"start": v(25, 2.74) * mm, "end": v(28, 2.74) * mm});
            skLineSegment(sketch, "E90.left", {"start": v(25, 12.74) * mm, "end": v(25, 2.74) * mm});
            skLineSegment(sketch, "E90.right", {"start": v(28, 12.74) * mm, "end": v(28, 2.74) * mm});
            skLineSegment(sketch, "E91.bottom", {"start": v(25, 32.74) * mm, "end": v(28, 32.74) * mm});
            skLineSegment(sketch, "E91.top", {"start": v(25, 22.74) * mm, "end": v(28, 22.74) * mm});
            skLineSegment(sketch, "E91.left", {"start": v(25, 32.74) * mm, "end": v(25, 22.74) * mm});
            skLineSegment(sketch, "E91.right", {"start": v(28, 32.74) * mm, "end": v(28, 22.74) * mm});
            skLineSegment(sketch, "E92.bottom", {"start": v(25, -7.26) * mm, "end": v(28, -7.26) * mm});
            skLineSegment(sketch, "E92.top", {"start": v(25, -17.26) * mm, "end": v(28, -17.26) * mm});
            skLineSegment(sketch, "E92.left", {"start": v(25, -7.26) * mm, "end": v(25, -17.26) * mm});
            skLineSegment(sketch, "E92.right", {"start": v(28, -7.26) * mm, "end": v(28, -17.26) * mm});
            skLineSegment(sketch, "E93", {"start": v(-26.5, 2.74) * mm, "end": v(-26.5, -7.26) * mm, "construction": true});
            skLineSegment(sketch, "E94", {"start": v(-26.5, 22.74) * mm, "end": v(-26.5, 12.74) * mm, "construction": true});
            skLineSegment(sketch, "E95", {"start": v(26.5, 22.74) * mm, "end": v(26.5, 12.74) * mm, "construction": true});
            skLineSegment(sketch, "E96", {"start": v(26.5, 2.74) * mm, "end": v(26.5, -7.26) * mm, "construction": true});
            skSolve(sketch);
        }
        {
            var Q0;
            Q0 = qSketchRegion(id + "F20", true);
            extrude(context, id + "F21", {"entities" : qUnion([Q0]), "depth" : 3 * mm});
        }
        {
            var Q0;
            Q0=qCreatedBy(makeId("Front.planeOp"),FACE);
            var sketch = newSketch(context, id + "F22", { "sketchPlane" : qUnion([Q0])});
            skLineSegment(sketch, "E97", {"start": v(-15, 25) * mm, "end": v(-14, 25) * mm});
            skLineSegment(sketch, "E98", {"start": v(-14, 25) * mm, "end": v(-14, 28) * mm});
            skLineSegment(sketch, "E99", {"start": v(-14, 28) * mm, "end": v(-6, 28) * mm});
            skLineSegment(sketch, "E100", {"start": v(-6, 28) * mm, "end": v(-6, 25) * mm});
            skLineSegment(sketch, "E101", {"start": v(-15, 25) * mm, "end": v(-15, 23) * mm});
            skLineSegment(sketch, "E102", {"start": v(-6, 25) * mm, "end": v(6, 25) * mm});
            skLineSegment(sketch, "E103", {"start": v(6, 25) * mm, "end": v(6, 28) * mm});
            skLineSegment(sketch, "E104", {"start": v(6, 28) * mm, "end": v(14, 28) * mm});
            skLineSegment(sketch, "E105", {"start": v(14, 28) * mm, "end": v(14, 25) * mm});
            skLineSegment(sketch, "E106", {"start": v(14, 25) * mm, "end": v(15, 25) * mm});
            skLineSegment(sketch, "E107", {"start": v(15, 25) * mm, "end": v(15, 23) * mm});
            skLineSegment(sketch, "E108", {"start": v(0, 25) * mm, "end": v(0, -25) * mm, "construction": true});
            skLineSegment(sketch, "E109", {"start": v(-6, -25) * mm, "end": v(6, -25) * mm});
            skLineSegment(sketch, "E110", {"start": v(6, -25) * mm, "end": v(6, -28) * mm});
            skLineSegment(sketch, "E111", {"start": v(6, -28) * mm, "end": v(14, -28) * mm});
            skLineSegment(sketch, "E112", {"start": v(14, -28) * mm, "end": v(14, -25) * mm});
            skLineSegment(sketch, "E113", {"start": v(14, -25) * mm, "end": v(15, -25) * mm});
            skLineSegment(sketch, "E114", {"start": v(15, -25) * mm, "end": v(15, -23) * mm});
            skLineSegment(sketch, "E115", {"start": v(-6, -25) * mm, "end": v(-6, -28) * mm});
            skLineSegment(sketch, "E116", {"start": v(-6, -28) * mm, "end": v(-14, -28) * mm});
            skLineSegment(sketch, "E117", {"start": v(-14, -28) * mm, "end": v(-14, -25) * mm});
            skLineSegment(sketch, "E118", {"start": v(-14, -25) * mm, "end": v(-15, -25) * mm});
            skLineSegment(sketch, "E119", {"start": v(-15, -25) * mm, "end": v(-15, -23) * mm});
            skLineSegment(sketch, "E120", {"start": v(-5, 0) * mm, "end": v(5, 0) * mm, "construction": true});
            skLineSegment(sketch, "E121", {"start": v(-5, 0) * mm, "end": v(-25, 0) * mm, "construction": true});
            skLineSegment(sketch, "E122", {"start": v(5, 0) * mm, "end": v(25, 0) * mm, "construction": true});
            skFitSpline(sketch, "E123", {"points": [v(-15, 23) * mm, v(-5, 0) * mm, v(-15, -23) * mm, v(-25, 0) * mm, v(-15, 23) * mm]});
            skFitSpline(sketch, "E124", {"points": [v(15, 23) * mm, v(5, 0) * mm, v(15, -23) * mm, v(25, 0) * mm, v(15, 23) * mm]});
            skSolve(sketch);
        }
        {
            var Q0;
            Q0 = qSketchRegion(id + "F22", true);
            extrude(context, id + "F23", {"entities" : qUnion([Q0]), "depth" : 3 * mm});
        }
        {
            var Q0;
            Q0=qCreatedBy(makeId("Front.planeOp"),FACE);
            var sketch = newSketch(context, id + "F24", { "sketchPlane" : qUnion([Q0])});
            skLineSegment(sketch, "E125", {"start": v(0, 21.5) * mm, "end": v(0, -21.5) * mm, "construction": true});
            skLineSegment(sketch, "E126", {"start": v(-55, -21.5) * mm, "end": v(55, -21.5) * mm});
            skLineSegment(sketch, "E127", {"start": v(-24, 21.5) * mm, "end": v(-16, 21.5) * mm});
            skLineSegment(sketch, "E128", {"start": v(-16, 21.5) * mm, "end": v(-16, 18.5) * mm});
            skLineSegment(sketch, "E129", {"start": v(-16, 18.5) * mm, "end": v(-4, 18.5) * mm});
            skLineSegment(sketch, "E130", {"start": v(-4, 18.5) * mm, "end": v(-4, 21.5) * mm});
            skLineSegment(sketch, "E131", {"start": v(-4, 21.5) * mm, "end": v(4, 21.5) * mm});
            skLineSegment(sketch, "E132", {"start": v(4, 21.5) * mm, "end": v(4, 18.5) * mm});
            skLineSegment(sketch, "E133", {"start": v(16, 18.5) * mm, "end": v(16, 21.5) * mm});
            skLineSegment(sketch, "E134", {"start": v(16, 21.5) * mm, "end": v(24, 21.5) * mm});
            skLineSegment(sketch, "E135", {"start": v(24, 21.5) * mm, "end": v(24, 18.5) * mm});
            skLineSegment(sketch, "E136", {"start": v(24, 18.5) * mm, "end": v(25, 18.5) * mm});
            skLineSegment(sketch, "E137", {"start": v(16, 18.5) * mm, "end": v(4, 18.5) * mm});
            skLineSegment(sketch, "E138", {"start": v(-24, 21.5) * mm, "end": v(-24, 18.5) * mm});
            skLineSegment(sketch, "E139", {"start": v(-24, 18.5) * mm, "end": v(-25, 18.5) * mm});
            skLineSegment(sketch, "E140", {"start": v(-25, 18.5) * mm, "end": v(-25, 16.5) * mm});
            skLineSegment(sketch, "E141", {"start": v(25, 18.5) * mm, "end": v(25, 16.5) * mm});
            skLineSegment(sketch, "E142", {"start": v(-55, -21.5) * mm, "end": v(-55, -18.5) * mm});
            skLineSegment(sketch, "E143", {"start": v(55, -21.5) * mm, "end": v(55, -18.5) * mm});
            skLineSegment(sketch, "E144", {"start": v(-15, 0) * mm, "end": v(15, 0) * mm, "construction": true});
            skLineSegment(sketch, "E145", {"start": v(-15, 0) * mm, "end": v(-105, 0) * mm, "construction": true});
            skLineSegment(sketch, "E146", {"start": v(15, 0) * mm, "end": v(105, 0) * mm, "construction": true});
            skFitSpline(sketch, "E147", {"points": [v(-25, 16.5) * mm, v(-15, 0) * mm, v(-55, -18.5) * mm, v(-105, 0) * mm, v(-25, 16.5) * mm]});
            skFitSpline(sketch, "E148", {"points": [v(25, 16.5) * mm, v(15, 0) * mm, v(55, -18.5) * mm, v(105, 0) * mm, v(25, 16.5) * mm]});
            skSolve(sketch);
        }
        {
            var Q0;
            Q0 = qSketchRegion(id + "F24", true);
            extrude(context, id + "F25", {"entities" : qUnion([Q0]), "depth" : 3 * mm});
        }
        {
            var Q0;
            Q0=qCreatedBy(makeId("Top.planeOp"),FACE);
            var sketch = newSketch(context, id + "F26", { "sketchPlane" : qUnion([Q0])});
            skArc(sketch, "E149.0", {"start": v(1.45, 9.71) * mm, "mid": v(0, 10.2) * mm, "end": v(-1.45, 9.71) * mm});
            skLineSegment(sketch, "E150.0", {"start": v(-1.45, 9.71) * mm, "end": v(-1.45, 5.77) * mm});
            skLineSegment(sketch, "E151.0", {"start": v(1.45, 9.71) * mm, "end": v(1.45, 5.77) * mm});
            skArc(sketch, "E152", {"start": v(6, 47.6) * mm, "mid": v(0, 53.74) * mm, "end": v(-6, 47.6) * mm});
            skArc(sketch, "E153", {"start": v(-5, 7.62) * mm, "mid": v(0, 2.74) * mm, "end": v(5, 7.61) * mm});
            skCircle(sketch, "E154", {"center": v(0, 47.74) * mm, "radius": 2.95 * mm});
            skLineSegment(sketch, "E155", {"start": v(-6, 47.6) * mm, "end": v(-5, 7.61) * mm});
            skLineSegment(sketch, "E156", {"start": v(5, 7.61) * mm, "end": v(6, 47.6) * mm});
            skArc(sketch, "E157.trimOffspring", {"start": v(-1.45, 5.77) * mm, "mid": v(0, 5.29) * mm, "end": v(1.45, 5.77) * mm});
            skSolve(sketch);
        }
        {
            var Q0;
            Q0 = qSketchRegion(id + "F26", true);
            extrude(context, id + "F27", {"entities" : qUnion([Q0]), "depth" : 3 * mm});
        }
    });
